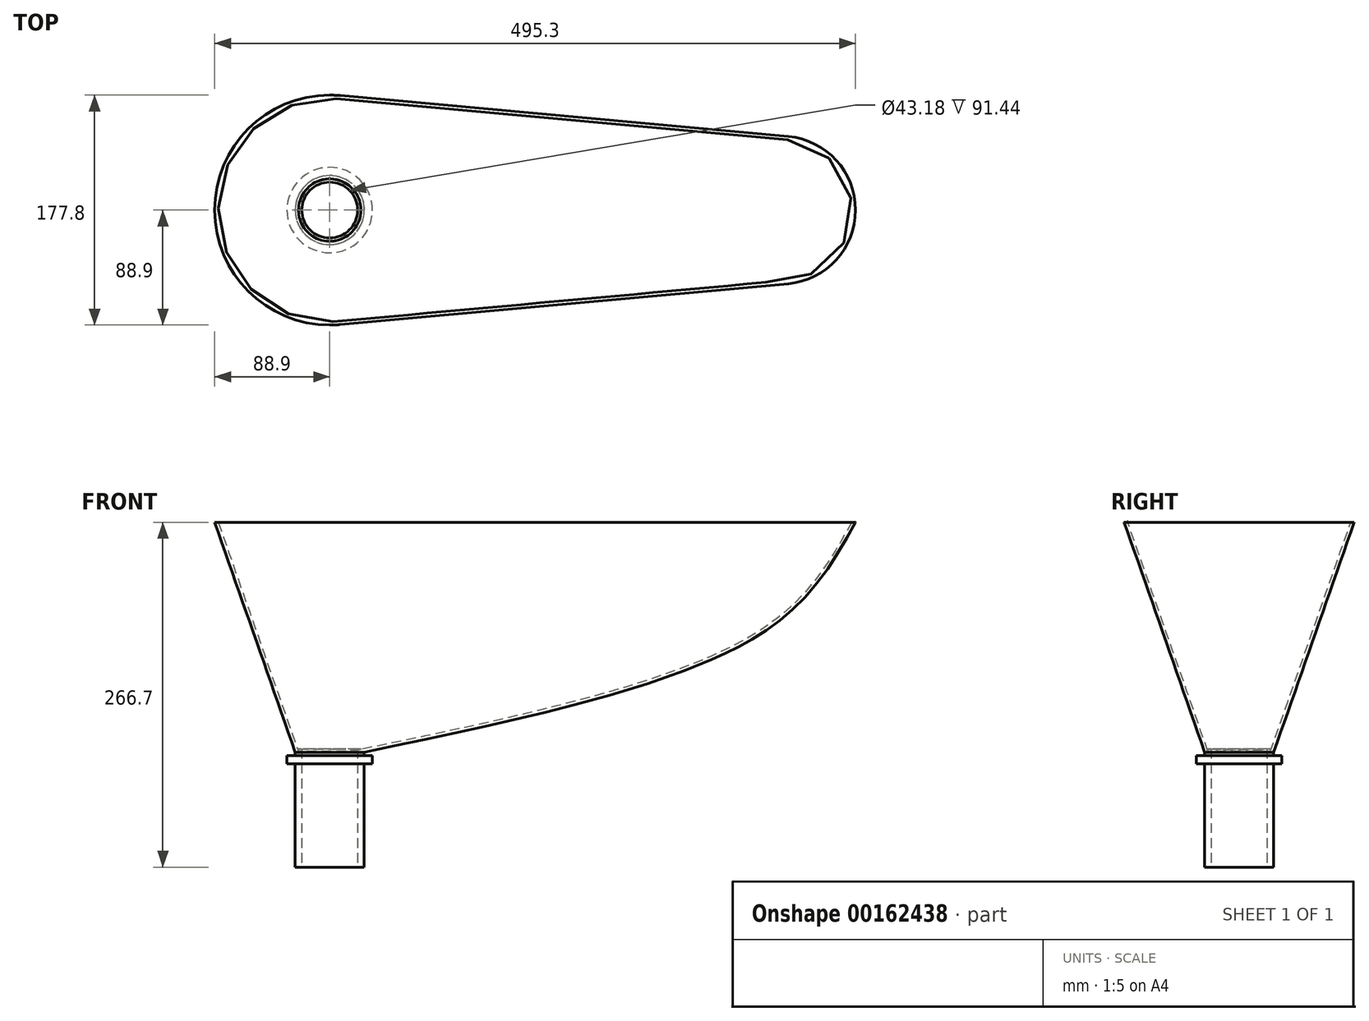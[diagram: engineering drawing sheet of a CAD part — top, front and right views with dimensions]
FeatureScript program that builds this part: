
annotation { "Feature Type Name" : "Feature", "Feature Type Description" : "" }
export const myFeature = defineFeature(function(context is Context, id is Id, definition is map)
    precondition{}
    {
        {
            var Q0;
            Q0=qCreatedBy(makeId("Top.planeOp"),FACE);
            var sketch = newSketch(context, id + "F0", { "sketchPlane" : qUnion([Q0])});
            skCircle(sketch, "E0", {"center": v(0, 0) * mm, "radius": 26.67 * mm});
            skCircle(sketch, "E1.0", {"center": v(0, 0) * mm, "radius": 21.59 * mm});
            skSolve(sketch);
        }
        {
            var Q0;
            Q0=qSketchRegion(id+"F0",true);
            extrude(context, id + "F1", {"entities" : qUnion([Q0]), "depth" : 76.2 * mm, "hasSecondDirection" : true, "secondDirectionOppositeDirection" : true, "secondDirectionDepth" : 12.7 * mm});
        }
        {
            var Q0;
            Q0=qCreatedBy(makeId("Top.planeOp"),FACE);
            cPlane(context, id + "F2", {"entities" : qUnion([Q0]), "cplaneType" : CPlaneType.OFFSET, "offset" : 254 * mm, "width" : 152.4 * mm, "height" : 152.4 * mm});
        }
        {
            var Q0;
            Q0=qCreatedBy(id+"F2.planeOp",FACE);
            var sketch = newSketch(context, id + "F3", { "sketchPlane" : qUnion([Q0])});
            skCircle(sketch, "E2", {"center": v(0, 0) * mm, "radius": 88.9 * mm});
            skCircle(sketch, "E3", {"center": v(349.25, 0) * mm, "radius": 57.15 * mm});
            skLineSegment(sketch, "E4", {"start": v(8.08, -88.53) * mm, "end": v(354.45, -56.91) * mm});
            skLineSegment(sketch, "E5", {"start": v(354.45, 56.91) * mm, "end": v(8.08, 88.53) * mm});
            skSolve(sketch);
        }
        {
            var Q0;
            Q0=makeQuery(id+"F1.opExtrude","CAP_FACE",FACE,{"disambiguationData":[OSD([sQuery(id+"F0.wireOp",EDGE,"E0"),sQuery(id+"F0.wireOp",EDGE,"E1.0")])],"isStart":false});
            var sketch = newSketch(context, id + "F4", { "sketchPlane" : qUnion([Q0])});
            skCircle(sketch, "E6.0", {"center": v(0, 0) * mm, "radius": 26.67 * mm});
            skSolve(sketch);
        }
        {
            var Q0;
            Q0=qCreatedBy(makeId("Right.planeOp"),FACE);
            var sketch = newSketch(context, id + "F5", { "sketchPlane" : qUnion([Q0])});
            skLineSegment(sketch, "E7.0", {"start": v(-26.67, 76.2) * mm, "end": v(26.67, 76.2) * mm, "construction": true});
            skLineSegment(sketch, "E8.0", {"start": v(-88.9, 254) * mm, "end": v(88.9, 254) * mm});
            skLineSegment(sketch, "E9", {"start": v(26.67, 76.2) * mm, "end": v(88.9, 254) * mm});
            skLineSegment(sketch, "E10", {"start": v(-26.67, 76.2) * mm, "end": v(-88.9, 254) * mm});
            skSolve(sketch);
        }
        {
            var Q0;
            Q0=qCreatedBy(makeId("Front.planeOp"),FACE);
            var sketch = newSketch(context, id + "F6", { "sketchPlane" : qUnion([Q0])});
            skLineSegment(sketch, "E11.0", {"start": v(-26.67, 76.2) * mm, "end": v(26.67, 76.2) * mm});
            skPoint(sketch, "E12.0", {"position": v(0, 254) * mm});
            skLineSegment(sketch, "E13", {"start": v(26.67, 76.2) * mm, "end": v(406.4, 254) * mm, "construction": true});
            skFitSpline(sketch, "E14", {"points": [v(26.67, 76.2) * mm, v(335.8, 169.32) * mm, v(406.4, 254) * mm], "startDerivative": vector(583.92, 121.66) * mm, "endDerivative": vector(136.4, 244.7) * mm});
            skSolve(sketch);
        }
        {
            var Q1;
            Q1=qSketchRegion(id+"F4",true);
            var Q2;
            Q2=qSketchRegion(id+"F3",true);
            var Q3;
            Q3=sQuery(id+"F5.wireOp",EDGE,"E9");
            var Q4;
            Q4=sQuery(id+"F5.wireOp",EDGE,"E10");
            var Q5;
            Q5=sQuery(id+"F6.wireOp",EDGE,"E14");
            loft(context, id + "F7", {"operationType" : NewBodyOperationType.ADD, "addGuides" : true, "sheetProfilesArray" : [{ "sheetProfileEntities" : qUnion([Q1]) }, { "sheetProfileEntities" : qUnion([Q2]) }], "guidesArray" : [{ "guideEntities" : qUnion([Q3]), "guideDerivativeType" : LoftGuideDerivativeType.DEFAULT, "guideDerivativeMagnitude" : 1 }, { "guideEntities" : qUnion([Q4]), "guideDerivativeType" : LoftGuideDerivativeType.DEFAULT, "guideDerivativeMagnitude" : 1 }, { "guideEntities" : qUnion([Q5]), "guideDerivativeType" : LoftGuideDerivativeType.DEFAULT, "guideDerivativeMagnitude" : 1 }]});
        }
        {
            var Q0;
            {var subQ0=sQuery(id+"F3.wireOp",EDGE,"E4");Q0=makeQuery(id+"F7.opLoft","CAP_FACE",FACE,{"disambiguationData":[OSD([makeQuery(id+"F3.imprint","IMPRINT",FACE,{"disambiguationData":[TD([[makeQuery(id+"F3.imprint","IMPRINT",EDGE,{"derivedFrom":subQ0}),1.0]])]})])],"isStart":true});}
            shell(context, id + "F8", {"entities" : qUnion([Q0]), "thickness" : 2.54 * mm});
        }
        {
            var Q0;
            Q0=makeQuery(id+"F7.opLoft","CAP_FACE",FACE,{"disambiguationData":[OSD([makeQuery(id+"F4.imprint","IMPRINT",FACE,{"disambiguationData":[TD([[makeQuery(id+"F4.imprint","IMPRINT",EDGE,{"derivedFrom":makeQuery(id+"F1.opExtrude","CAP_EDGE",EDGE,{"disambiguationData":[OSD([sQuery(id+"F0.wireOp",EDGE,"E1.0")])],"isStart":false})}),1.0]])]})])],"isStart":true});
            var sketch = newSketch(context, id + "F9", { "sketchPlane" : qUnion([Q0])});
            skCircle(sketch, "E15.0", {"center": v(0, 0) * mm, "radius": 21.59 * mm});
            skSolve(sketch);
        }
        {
            var Q0;
            Q0=qSketchRegion(id+"F9",true);
            extrude(context, id + "F10", {"entities" : qUnion([Q0]), "operationType" : NewBodyOperationType.REMOVE, "endBound" : BoundingType.THROUGH_ALL, "oppositeDirection" : true, "depth" : 25.4 * mm});
        }
        {
            var Q0;
            Q0=makeQuery(id+"F1.opExtrude","CAP_FACE",FACE,{"disambiguationData":[OSD([sQuery(id+"F0.wireOp",EDGE,"E0"),sQuery(id+"F0.wireOp",EDGE,"E1.0")])],"isStart":true});
            cPlane(context, id + "F11", {"entities" : qUnion([Q0]), "cplaneType" : CPlaneType.OFFSET, "offset" : 86.36 * mm, "oppositeDirection" : true, "width" : 152.4 * mm, "height" : 152.4 * mm});
        }
        {
            var Q0;
            Q0=qCreatedBy(id+"F11.planeOp",FACE);
            var sketch = newSketch(context, id + "F12", { "sketchPlane" : qUnion([Q0])});
            skPoint(sketch, "E16.0", {"position": v(0, 0) * mm});
            skCircle(sketch, "E17", {"center": v(0, 0) * mm, "radius": 33.02 * mm});
            skCircle(sketch, "E18.0", {"center": v(0, 0) * mm, "radius": 24.13 * mm});
            skSolve(sketch);
        }
        {
            var Q0;
            Q0=qSketchRegion(id+"F12",true);
            extrude(context, id + "F13", {"entities" : qUnion([Q0]), "operationType" : NewBodyOperationType.ADD, "depth" : 6.35 * mm});
        }
    });
